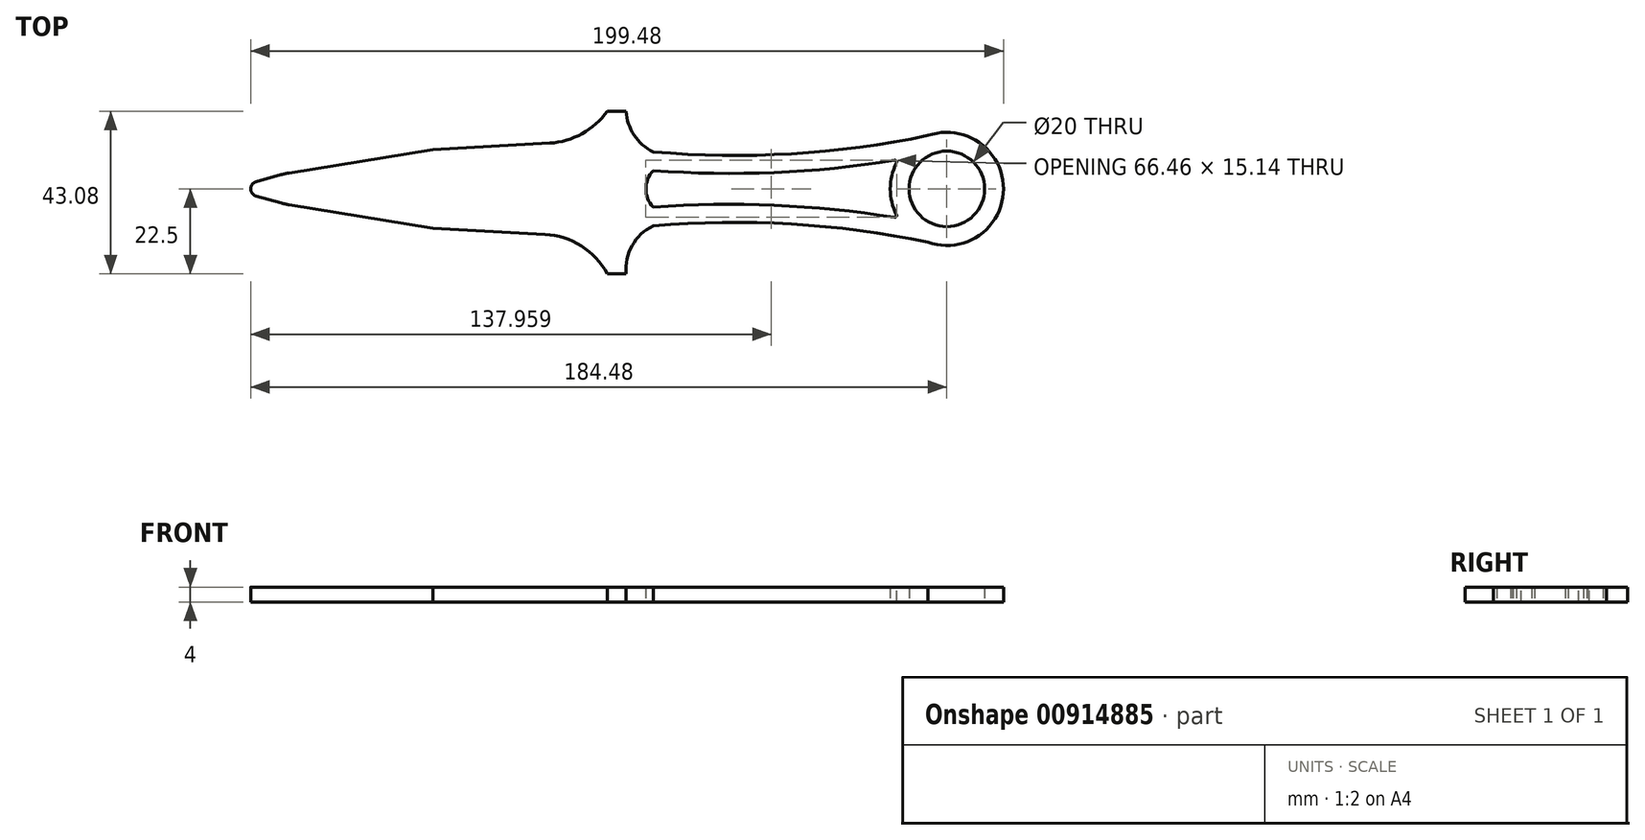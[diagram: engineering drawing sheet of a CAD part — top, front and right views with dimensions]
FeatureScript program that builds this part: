
annotation { "Feature Type Name" : "Feature", "Feature Type Description" : "" }
export const myFeature = defineFeature(function(context is Context, id is Id, definition is map)
    precondition{}
    {
        {
            var Q0;
            Q0=qCreatedBy(makeId("Top.planeOp"),FACE);
            var sketch = newSketch(context, id + "F0", { "sketchPlane" : qUnion([Q0])});
            skLineSegment(sketch, "E0.bottom", {"start": v(50, 12.96) * mm, "end": v(-16.14, 9.35) * mm});
            skPoint(sketch, "E0.middle", {"position": v(0, 0) * mm});
            skPoint(sketch, "E1", {"position": v(-50, 0) * mm});
            skLineSegment(sketch, "E2", {"start": v(-50, 0) * mm, "end": v(-16.14, 9.35) * mm});
            skPoint(sketch, "E3.trimOffspring.end.orphan", {"position": v(-50, 12.96) * mm});
            skPoint(sketch, "E4.orphan", {"position": v(-50, -12.96) * mm});
            skLineSegment(sketch, "E5.bottom", {"start": v(50, 20.58) * mm, "end": v(55, 20.58) * mm});
            skLineSegment(sketch, "E5.top", {"start": v(50, -22.5) * mm, "end": v(55, -22.5) * mm});
            skLineSegment(sketch, "E5.left", {"start": v(50, 20.58) * mm, "end": v(50, 12.96) * mm});
            skArc(sketch, "E6", {"start": v(55, 20.58) * mm, "mid": v(57.12, 14.2) * mm, "end": v(62.2, 9.8) * mm});
            skLineSegment(sketch, "E7", {"start": v(62.2, -9.8) * mm, "end": v(62.2, 9.8) * mm, "construction": true});
            skArc(sketch, "E8", {"start": v(62.2, -9.8) * mm, "mid": v(56.6, -15.01) * mm, "end": v(55, -22.5) * mm});
            skArc(sketch, "E9", {"start": v(62.2, 9.8) * mm, "mid": v(98.76, 9.3) * mm, "end": v(135, 14.14) * mm});
            skArc(sketch, "E10", {"start": v(135, -14.14) * mm, "mid": v(98.76, -9.3) * mm, "end": v(62.2, -9.8) * mm});
            skArc(sketch, "E11.0", {"start": v(62.2, 4.83) * mm, "mid": v(60.25, 0) * mm, "end": v(62.2, -4.83) * mm});
            skArc(sketch, "E12", {"start": v(62.2, 4.83) * mm, "mid": v(94.76, 4.36) * mm, "end": v(127.15, 7.73) * mm});
            skArc(sketch, "E13", {"start": v(127.15, -7.73) * mm, "mid": v(94.76, -4.36) * mm, "end": v(62.2, -4.83) * mm});
            skLineSegment(sketch, "E14.trimOffspring", {"start": v(50, -12.96) * mm, "end": v(50, -22.5) * mm});
            skPoint(sketch, "E15.center.orphan", {"position": v(62.2, 0) * mm});
            skCircle(sketch, "E16.converted", {"center": v(140, 0) * mm, "radius": 10 * mm});
            skArc(sketch, "E17.converted", {"start": v(127.15, 7.73) * mm, "mid": v(125, 0) * mm, "end": v(127.15, -7.73) * mm});
            skPoint(sketch, "E18.orphan", {"position": v(137, 9.54) * mm});
            skPoint(sketch, "E19.orphan", {"position": v(137, -9.54) * mm});
            skArc(sketch, "E20.trimOffspring", {"start": v(135, -14.14) * mm, "mid": v(155, 0) * mm, "end": v(135, 14.14) * mm});
            skLineSegment(sketch, "E21", {"start": v(-50, 0) * mm, "end": v(140, 0) * mm, "construction": true});
            skLineSegment(sketch, "E22.MirrorCS", {"start": v(-50, 0) * mm, "end": v(-16.14, -9.35) * mm});
            skLineSegment(sketch, "E23.MirrorCS", {"start": v(50, -12.96) * mm, "end": v(-16.14, -9.35) * mm});
            skSolve(sketch);
        }
        {
            var Q0;
            Q0=qSketchRegion(id+"F0",true);
            extrude(context, id + "F1", {"entities" : qUnion([Q0]), "depth" : 4 * mm, "offsetDistance" : 25 * mm});
        }
        {
            var Q0;
            Q0=makeQuery(id+"F1.opExtrude","SWEPT_EDGE",EDGE,{"disambiguationData":[OSD([sQuery(id+"F0.wireOp",EDGE,"E12"),sQuery(id+"F0.wireOp",EDGE,"E17.converted")])]});
            var Q1;
            Q1=makeQuery(id+"F1.opExtrude","SWEPT_EDGE",EDGE,{"disambiguationData":[OSD([sQuery(id+"F0.wireOp",EDGE,"E13"),sQuery(id+"F0.wireOp",EDGE,"E17.converted")])]});
            fillet(context, id + "F2", {"entities" : qUnion([Q0, Q1]), "radius" : 0.5 * mm, "tangentPropagation" : true, "allowEdgeOverflow" : false});
        }
        {
            var Q0;
            Q0=makeQuery(id+"F1.opExtrude","SWEPT_EDGE",EDGE,{"disambiguationData":[OSD([sQuery(id+"F0.wireOp",EDGE,"E2"),sQuery(id+"F0.wireOp",EDGE,"E22.MirrorCS")])]});
            fillet(context, id + "F3", {"entities" : qUnion([Q0]), "radius" : 2 * mm, "tangentPropagation" : true, "allowEdgeOverflow" : false});
        }
        {
            var Q0;
            Q0=makeQuery(id+"F1.opExtrude","SWEPT_EDGE",EDGE,{"disambiguationData":[OSD([sQuery(id+"F0.wireOp",EDGE,"E0.bottom"),sQuery(id+"F0.wireOp",EDGE,"E5.left")])]});
            var Q1;
            Q1=makeQuery(id+"F1.opExtrude","SWEPT_EDGE",EDGE,{"disambiguationData":[OSD([sQuery(id+"F0.wireOp",EDGE,"E14.trimOffspring"),sQuery(id+"F0.wireOp",EDGE,"E23.MirrorCS")])]});
            fillet(context, id + "F4", {"entities" : qUnion([Q0, Q1]), "radius" : 20 * mm, "tangentPropagation" : true, "allowEdgeOverflow" : false});
        }
        {
            var Q0;
            Q0=makeQuery(id+"F1.opExtrude","SWEPT_EDGE",EDGE,{"disambiguationData":[OSD([sQuery(id+"F0.wireOp",EDGE,"E22.MirrorCS"),sQuery(id+"F0.wireOp",EDGE,"E23.MirrorCS")])]});
            var Q1;
            Q1=makeQuery(id+"F1.opExtrude","SWEPT_EDGE",EDGE,{"disambiguationData":[OSD([sQuery(id+"F0.wireOp",EDGE,"E0.bottom"),sQuery(id+"F0.wireOp",EDGE,"E2")])]});
            chamfer(context, id + "F5", {"entities" : qUnion([Q0, Q1]), "width" : 20 * mm, "tangentPropagation" : true});
        }
        {
            var Q0;
            {var subQ0=sQuery(id+"F0.wireOp",EDGE,"E2");Q0=makeQuery(id+"F5.opChamfer","BLEND_EDGE",EDGE,{"blendedFrom":[makeQuery(id+"F1.opExtrude","SWEPT_EDGE",EDGE,{"disambiguationData":[OSD([sQuery(id+"F0.wireOp",EDGE,"E0.bottom"),subQ0])]}),makeQuery(id+"F1.opExtrude","SWEPT_FACE",FACE,{"disambiguationData":[OSD([subQ0])]})],"blendedInto":[makeQuery(id+"F1.opExtrude","SWEPT_FACE",FACE,{"disambiguationData":[OSD([subQ0])]})]});}
            var Q1;
            {var subQ0=sQuery(id+"F0.wireOp",EDGE,"E22.MirrorCS");Q1=makeQuery(id+"F5.opChamfer","BLEND_EDGE",EDGE,{"blendedFrom":[makeQuery(id+"F1.opExtrude","SWEPT_EDGE",EDGE,{"disambiguationData":[OSD([subQ0,sQuery(id+"F0.wireOp",EDGE,"E23.MirrorCS")])]}),makeQuery(id+"F1.opExtrude","SWEPT_FACE",FACE,{"disambiguationData":[OSD([subQ0])]})],"blendedInto":[makeQuery(id+"F1.opExtrude","SWEPT_FACE",FACE,{"disambiguationData":[OSD([subQ0])]})]});}
            fillet(context, id + "F6", {"entities" : qUnion([Q0, Q1]), "radius" : 20 * mm, "tangentPropagation" : true, "allowEdgeOverflow" : false});
        }
    });
